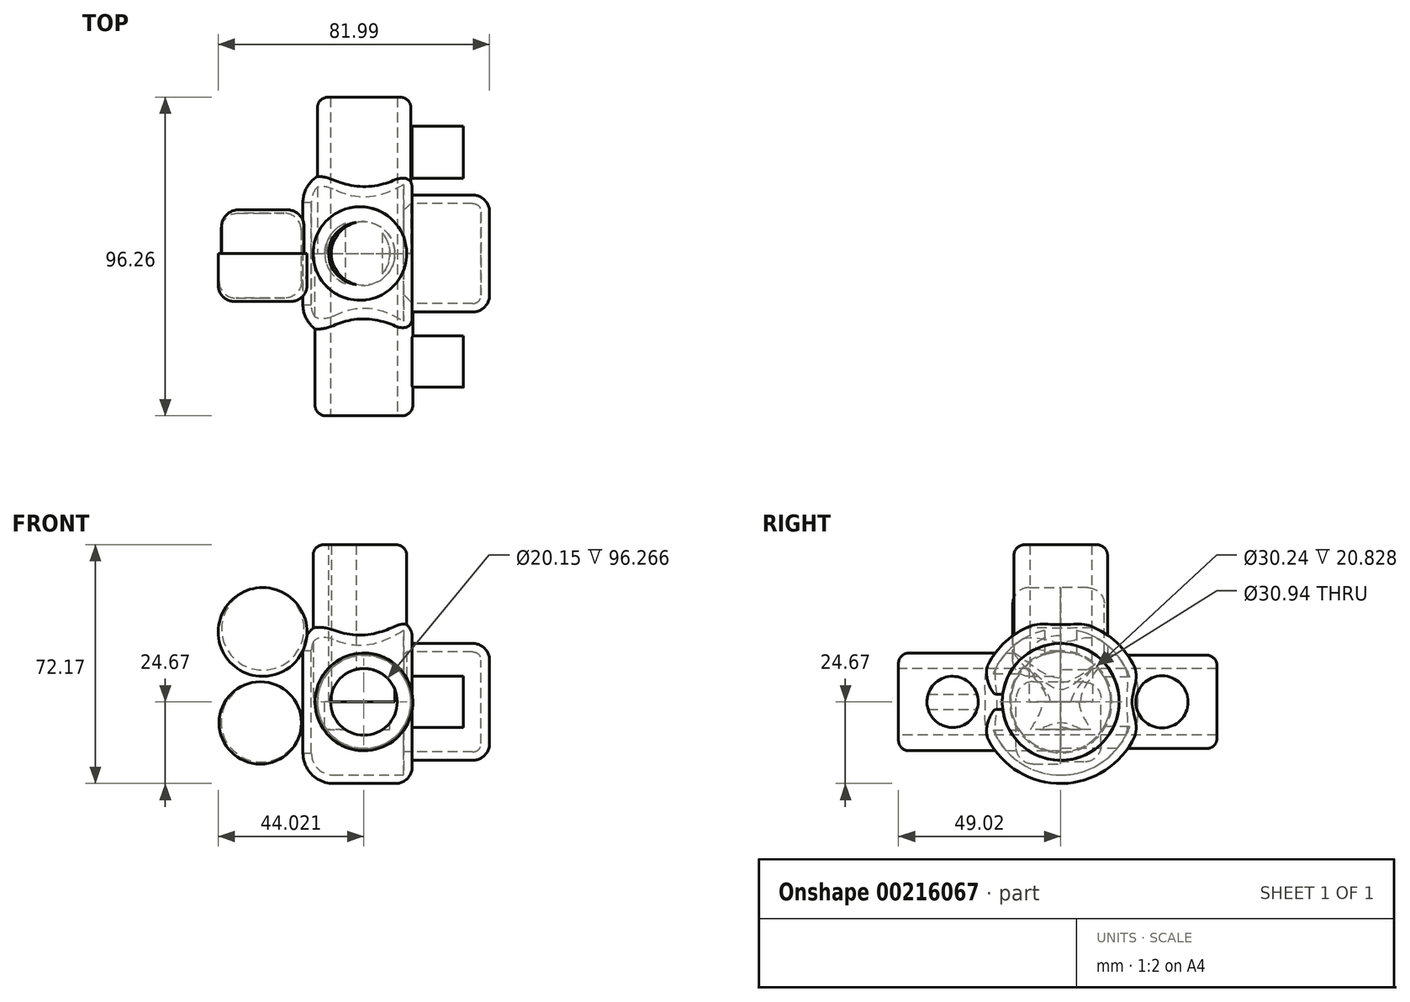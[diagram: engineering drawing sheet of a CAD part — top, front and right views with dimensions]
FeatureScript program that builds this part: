
annotation { "Feature Type Name" : "Feature", "Feature Type Description" : "" }
export const myFeature = defineFeature(function(context is Context, id is Id, definition is map)
    precondition{}
    {
        {
            var Q0;
            Q0=qCreatedBy(makeId("Right.planeOp"),FACE);
            var sketch = newSketch(context, id + "F0", { "sketchPlane" : qUnion([Q0])});
            skCircle(sketch, "E0", {"center": v(0, 0) * mm, "radius": 17.66 * mm});
            skSolve(sketch);
        }
        {
            var Q0;
            Q0 = qSketchRegion(id + "F0", true);
            extrude(context, id + "F1", {"entities" : qUnion([Q0]), "depth" : 23.37 * mm});
        }
        {
            var Q0;
            Q0=makeQuery(id+"F1.opExtrude","CAP_EDGE",EDGE,{"disambiguationData":[OSD([sQuery(id+"F0.wireOp",EDGE,"E0")])],"isStart":false});
            fillet(context, id + "F2", {"entities" : qUnion([Q0]), "radius" : 5.08 * mm, "tangentPropagation" : true, "allowEdgeOverflow" : false});
        }
        {
            var Q0;
            Q0=qCreatedBy(makeId("Right.planeOp"),FACE);
            var sketch = newSketch(context, id + "F3", { "sketchPlane" : qUnion([Q0])});
            skCircle(sketch, "E1", {"center": v(0, 0) * mm, "radius": 24.67 * mm});
            skSolve(sketch);
        }
        {
            var Q0;
            Q0 = qSketchRegion(id + "F3", true);
            extrude(context, id + "F4", {"entities" : qUnion([Q0]), "operationType" : NewBodyOperationType.ADD, "oppositeDirection" : true, "depth" : 33.02 * mm});
        }
        {
            var Q0;
            Q0=makeQuery(id+"F4.opExtrude","CAP_EDGE",EDGE,{"disambiguationData":[OSD([sQuery(id+"F3.wireOp",EDGE,"E1")])],"isStart":false});
            fillet(context, id + "F5", {"entities" : qUnion([Q0]), "radius" : 9.2 * mm, "tangentPropagation" : true, "allowEdgeOverflow" : false});
        }
        {
            var Q0;
            Q0=makeQuery(id+"F4.opExtrude","CAP_FACE",FACE,{"disambiguationData":[OSD([sQuery(id+"F3.wireOp",EDGE,"E1")])],"isStart":false});
            shell(context, id + "F6", {"entities" : qUnion([Q0]), "thickness" : 2.54 * mm});
        }
        {
            var Q0;
            Q0=makeQuery(id+"F4.opExtrude","CAP_EDGE",EDGE,{"disambiguationData":[OSD([sQuery(id+"F3.wireOp",EDGE,"E1")])],"isStart":true});
            fillet(context, id + "F7", {"entities" : qUnion([Q0]), "radius" : 5.08 * mm, "tangentPropagation" : true, "allowEdgeOverflow" : false});
        }
        {
            var Q0;
            Q0=qCreatedBy(makeId("Front.planeOp"),FACE);
            var sketch = newSketch(context, id + "F8", { "sketchPlane" : qUnion([Q0])});
            skArc(sketch, "E2", {"start": v(-31.12, -19.32) * mm, "mid": v(-5.42, -33.5) * mm, "end": v(18.67, -16.73) * mm});
            skArc(sketch, "E3", {"start": v(18.15, 17.77) * mm, "mid": v(-5.43, 34.32) * mm, "end": v(-31.9, 22.95) * mm});
            skArc(sketch, "E4", {"start": v(-31.9, 22.95) * mm, "mid": v(-58.62, 21.14) * mm, "end": v(-31.9, 19.32) * mm});
            skCircle(sketch, "E5", {"center": v(-45.2, 21.14) * mm, "radius": 13.42 * mm});
            skSolve(sketch);
        }
        {
            var Q0;
            Q0=makeQuery(id+"F8.imprint","IMPRINT",FACE,{"disambiguationData":[TD([[makeQuery(id+"F8.imprint","IMPRINT",EDGE,{"derivedFrom":sQuery(id+"F8.wireOp",EDGE,"E5")}),1.0]])]});
            extrude(context, id + "F9", {"entities" : qUnion([Q0]), "operationType" : NewBodyOperationType.ADD, "depth" : 14.48 * mm});
        }
        {
            var Q0;
            Q0=makeQuery(id+"F9.opExtrude","CAP_EDGE",EDGE,{"disambiguationData":[OSD([sQuery(id+"F8.wireOp",EDGE,"E5")])],"isStart":false});
            fillet(context, id + "F10", {"entities" : qUnion([Q0]), "radius" : 4.9 * mm, "tangentPropagation" : true, "allowEdgeOverflow" : false});
        }
        {
            var Q0;
            Q0=qCreatedBy(makeId("Front.planeOp"),FACE);
            var sketch = newSketch(context, id + "F11", { "sketchPlane" : qUnion([Q0])});
            skCircle(sketch, "E6", {"center": v(-45.13, 22.07) * mm, "radius": 12.46 * mm});
            skSolve(sketch);
        }
        {
            var Q0;
            Q0=makeQuery(id+"F11.imprint","IMPRINT",FACE,{"disambiguationData":[TD([[makeQuery(id+"F11.imprint","IMPRINT",EDGE,{"derivedFrom":sQuery(id+"F11.wireOp",EDGE,"E6")}),1.0]])]});
            extrude(context, id + "F12", {"entities" : qUnion([Q0]), "operationType" : NewBodyOperationType.ADD, "oppositeDirection" : true, "depth" : 13.2 * mm});
        }
        {
            var Q0;
            Q0=makeQuery(id+"F12.opExtrude","CAP_EDGE",EDGE,{"disambiguationData":[OSD([sQuery(id+"F11.wireOp",EDGE,"E6")])],"isStart":false});
            fillet(context, id + "F13", {"entities" : qUnion([Q0]), "radius" : 5.08 * mm, "tangentPropagation" : true, "allowEdgeOverflow" : false});
        }
        {
            var Q0;
            Q0=qCreatedBy(makeId("Front.planeOp"),FACE);
            var sketch = newSketch(context, id + "F14", { "sketchPlane" : qUnion([Q0])});
            skCircle(sketch, "E7", {"center": v(-45.9, -6.35) * mm, "radius": 12.45 * mm});
            skSolve(sketch);
        }
        {
            var Q0;
            Q0=makeQuery(id+"F14.imprint","IMPRINT",FACE,{"disambiguationData":[TD([[makeQuery(id+"F14.imprint","IMPRINT",EDGE,{"derivedFrom":sQuery(id+"F14.wireOp",EDGE,"E7")}),1.0]])]});
            extrude(context, id + "F15", {"entities" : qUnion([Q0]), "depth" : 13.46 * mm});
        }
        {
            var Q0;
            Q0=makeQuery(id+"F15.opExtrude","CAP_FACE",FACE,{"disambiguationData":[OSD([sQuery(id+"F14.wireOp",EDGE,"E7")])],"isStart":false});
            fillet(context, id + "F16", {"entities" : qUnion([Q0]), "radius" : 5.08 * mm, "tangentPropagation" : true, "allowEdgeOverflow" : false});
        }
        {
            var Q0;
            Q0=qCreatedBy(makeId("Front.planeOp"),FACE);
            var sketch = newSketch(context, id + "F17", { "sketchPlane" : qUnion([Q0])});
            skCircle(sketch, "E8", {"center": v(-45.65, -6.1) * mm, "radius": 12.07 * mm});
            skSolve(sketch);
        }
        {
            var Q0;
            Q0=makeQuery(id+"F17.imprint","IMPRINT",FACE,{"disambiguationData":[TD([[makeQuery(id+"F17.imprint","IMPRINT",EDGE,{"derivedFrom":sQuery(id+"F17.wireOp",EDGE,"E8")}),1.0]])]});
            extrude(context, id + "F18", {"entities" : qUnion([Q0]), "operationType" : NewBodyOperationType.ADD, "oppositeDirection" : true, "depth" : 12.2 * mm});
        }
        {
            var Q0;
            Q0=makeQuery(id+"F18.opExtrude","CAP_EDGE",EDGE,{"disambiguationData":[OSD([sQuery(id+"F17.wireOp",EDGE,"E8")])],"isStart":false});
            fillet(context, id + "F19", {"entities" : qUnion([Q0]), "radius" : 5.08 * mm, "tangentPropagation" : true, "allowEdgeOverflow" : false});
        }
        {
            var Q0;
            Q0=qCreatedBy(makeId("Top.planeOp"),FACE);
            var sketch = newSketch(context, id + "F20", { "sketchPlane" : qUnion([Q0])});
            skCircle(sketch, "E9", {"center": v(-15.82, 0) * mm, "radius": 14.14 * mm});
            skSolve(sketch);
        }
        {
            var Q0;
            Q0 = qSketchRegion(id + "F20", true);
            extrude(context, id + "F21", {"entities" : qUnion([Q0]), "operationType" : NewBodyOperationType.ADD, "depth" : 47.5 * mm});
        }
        {
            var Q0;
            Q0=makeQuery(id+"F21.opExtrude","CAP_EDGE",EDGE,{"disambiguationData":[OSD([sQuery(id+"F20.wireOp",EDGE,"E9")])],"isStart":false});
            fillet(context, id + "F22", {"entities" : qUnion([Q0]), "radius" : 3.17 * mm, "tangentPropagation" : true, "allowEdgeOverflow" : false});
        }
        {
            var Q0;
            Q0=qCreatedBy(makeId("Front.planeOp"),FACE);
            var sketch = newSketch(context, id + "F23", { "sketchPlane" : qUnion([Q0])});
            skCircle(sketch, "E10", {"center": v(-14.52, 0) * mm, "radius": 14.12 * mm});
            skSolve(sketch);
        }
        {
            var Q0;
            Q0 = qSketchRegion(id + "F23", true);
            extrude(context, id + "F24", {"entities" : qUnion([Q0]), "operationType" : NewBodyOperationType.ADD, "oppositeDirection" : true, "depth" : 47.24 * mm});
        }
        {
            var Q0;
            Q0=qCreatedBy(makeId("Front.planeOp"),FACE);
            var sketch = newSketch(context, id + "F25", { "sketchPlane" : qUnion([Q0])});
            skCircle(sketch, "E11", {"center": v(-14.6, 0) * mm, "radius": 14.78 * mm});
            skSolve(sketch);
        }
        {
            var Q0;
            Q0 = qSketchRegion(id + "F25", true);
            extrude(context, id + "F26", {"entities" : qUnion([Q0]), "operationType" : NewBodyOperationType.ADD, "depth" : 49.02 * mm});
        }
        {
            var Q0;
            Q0=qCreatedBy(makeId("Right.planeOp"),FACE);
            var sketch = newSketch(context, id + "F27", { "sketchPlane" : qUnion([Q0])});
            skCircle(sketch, "E12", {"center": v(-32.68, 0) * mm, "radius": 7.73 * mm});
            skCircle(sketch, "E13", {"center": v(30.6, 0) * mm, "radius": 7.88 * mm});
            skSolve(sketch);
        }
        {
            var Q0;
            Q0 = qSketchRegion(id + "F27", true);
            extrude(context, id + "F28", {"entities" : qUnion([Q0]), "operationType" : NewBodyOperationType.ADD, "depth" : 15.5 * mm});
        }
        {
            var Q0;
            Q0=makeQuery(id+"F26.opExtrude","CAP_EDGE",EDGE,{"disambiguationData":[OSD([sQuery(id+"F25.wireOp",EDGE,"E11")])],"isStart":false});
            var Q1;
            Q1=makeQuery(id+"F24.opExtrude","CAP_EDGE",EDGE,{"disambiguationData":[OSD([sQuery(id+"F23.wireOp",EDGE,"E10")])],"isStart":false});
            fillet(context, id + "F29", {"entities" : qUnion([Q0, Q1]), "radius" : 3.17 * mm, "tangentPropagation" : true, "allowEdgeOverflow" : false});
        }
        {
            var Q0;
            Q0=makeQuery(id+"F26.opExtrude","CAP_FACE",FACE,{"disambiguationData":[OSD([sQuery(id+"F25.wireOp",EDGE,"E11")])],"isStart":false});
            var sketch = newSketch(context, id + "F30", { "sketchPlane" : qUnion([Q0])});
            skCircle(sketch, "E14.0", {"center": v(-14.6, 0) * mm, "radius": 10.08 * mm});
            skSolve(sketch);
        }
        {
            var Q0;
            Q0=makeQuery(id+"F30.imprint","IMPRINT",FACE,{"disambiguationData":[TD([[makeQuery(id+"F30.imprint","IMPRINT",EDGE,{"derivedFrom":sQuery(id+"F30.wireOp",EDGE,"E14.0")}),1.0]])]});
            extrude(context, id + "F31", {"entities" : qUnion([Q0]), "operationType" : NewBodyOperationType.REMOVE, "endBound" : BoundingType.THROUGH_ALL, "oppositeDirection" : true, "depth" : 25.4 * mm});
        }
        {
            var Q0;
            Q0=qCreatedBy(makeId("Top.planeOp"),FACE);
            var sketch = newSketch(context, id + "F32", { "sketchPlane" : qUnion([Q0])});
            skCircle(sketch, "E15", {"center": v(-16.6, 0) * mm, "radius": 9.81 * mm});
            skSolve(sketch);
        }
        {
            var Q0;
            Q0 = qSketchRegion(id + "F32", true);
            extrude(context, id + "F33", {"entities" : qUnion([Q0]), "operationType" : NewBodyOperationType.REMOVE, "oppositeDirection" : true, "depth" : 8.38 * mm});
        }
        {
            var Q0;
            Q0=makeQuery(id+"F21.opExtrude","CAP_FACE",FACE,{"disambiguationData":[OSD([sQuery(id+"F20.wireOp",EDGE,"E9")])],"isStart":false});
            var sketch = newSketch(context, id + "F34", { "sketchPlane" : qUnion([Q0])});
            skCircle(sketch, "E16.0", {"center": v(-15.82, 0) * mm, "radius": 9.44 * mm});
            skSolve(sketch);
        }
        {
            var Q0;
            Q0=makeQuery(id+"F34.imprint","IMPRINT",FACE,{"disambiguationData":[TD([[makeQuery(id+"F34.imprint","IMPRINT",EDGE,{"derivedFrom":sQuery(id+"F34.wireOp",EDGE,"E16.0")}),1.0]])]});
            extrude(context, id + "F35", {"entities" : qUnion([Q0]), "operationType" : NewBodyOperationType.REMOVE, "endBound" : BoundingType.UP_TO_NEXT, "oppositeDirection" : true, "depth" : 49.28 * mm});
        }
        {
            var Q0;
            Q0=qCreatedBy(makeId("Top.planeOp"),FACE);
            var sketch = newSketch(context, id + "F36", { "sketchPlane" : qUnion([Q0])});
            skCircle(sketch, "E17", {"center": v(-14.82, 0) * mm, "radius": 9.61 * mm});
            skSolve(sketch);
        }
        {
            var Q0;
            Q0=makeQuery(id+"F36.imprint","IMPRINT",FACE,{"disambiguationData":[TD([[makeQuery(id+"F36.imprint","IMPRINT",EDGE,{"derivedFrom":sQuery(id+"F36.wireOp",EDGE,"E17")}),1.0]])]});
            extrude(context, id + "F37", {"entities" : qUnion([Q0]), "operationType" : NewBodyOperationType.ADD, "depth" : 47.5 * mm});
        }
    });
